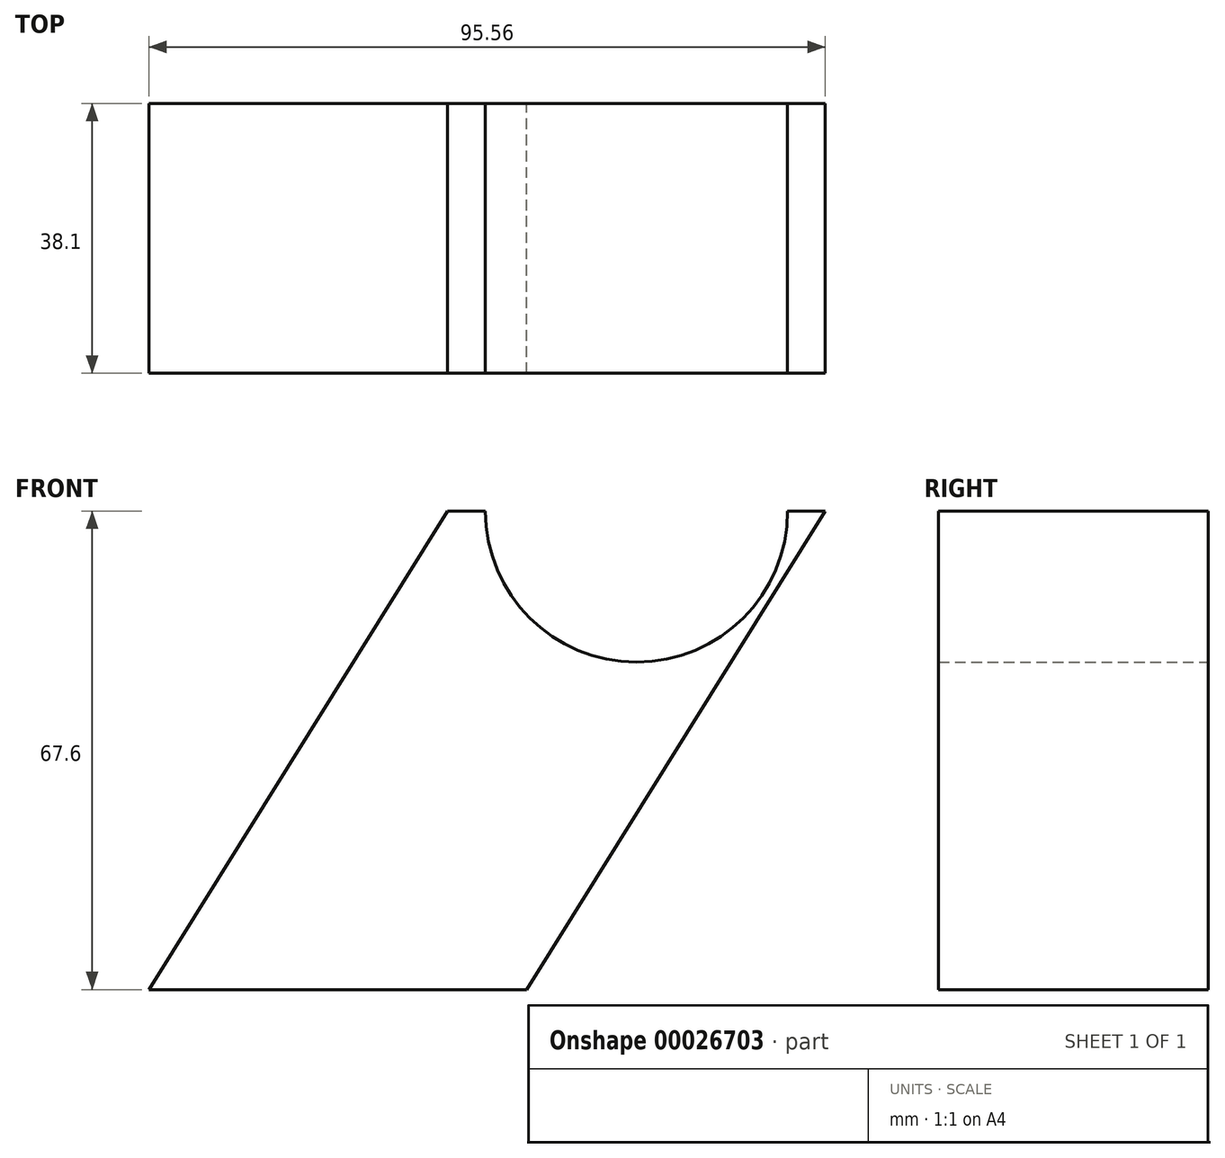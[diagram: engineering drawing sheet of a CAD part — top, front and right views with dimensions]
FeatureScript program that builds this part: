
annotation { "Feature Type Name" : "Feature", "Feature Type Description" : "" }
export const myFeature = defineFeature(function(context is Context, id is Id, definition is map)
    precondition{}
    {
        {
            var Q0;
            Q0=qCreatedBy(makeId("Front.planeOp"),FACE);
            var sketch = newSketch(context, id + "F0", { "sketchPlane" : qUnion([Q0])});
            skLineSegment(sketch, "E0", {"start": v(-95.56, -10.32) * mm, "end": v(-53.34, 57.28) * mm});
            skLineSegment(sketch, "E1", {"start": v(-95.56, -10.32) * mm, "end": v(-42.22, -10.32) * mm});
            skLineSegment(sketch, "E2", {"start": v(-42.22, -10.32) * mm, "end": v(0, 57.28) * mm});
            skLineSegment(sketch, "E3", {"start": v(0, 57.28) * mm, "end": v(-5.33, 57.28) * mm});
            skArc(sketch, "E4", {"start": v(-48, 57.28) * mm, "mid": v(-26.67, 35.94) * mm, "end": v(-5.33, 57.28) * mm});
            skLineSegment(sketch, "E5.trimOffspring", {"start": v(-48, 57.28) * mm, "end": v(-53.34, 57.28) * mm});
            skSolve(sketch);
        }
        {
            var Q0;
            Q0=makeQuery(id+"F0.imprint","IMPRINT",FACE,{"disambiguationData":[TD([[makeQuery(id+"F0.imprint","IMPRINT",EDGE,{"derivedFrom":sQuery(id+"F0.wireOp",EDGE,"E0")}),-1.0]])]});
            extrude(context, id + "F1", {"entities" : qUnion([Q0]), "depth" : 38.1 * mm});
        }
    });
